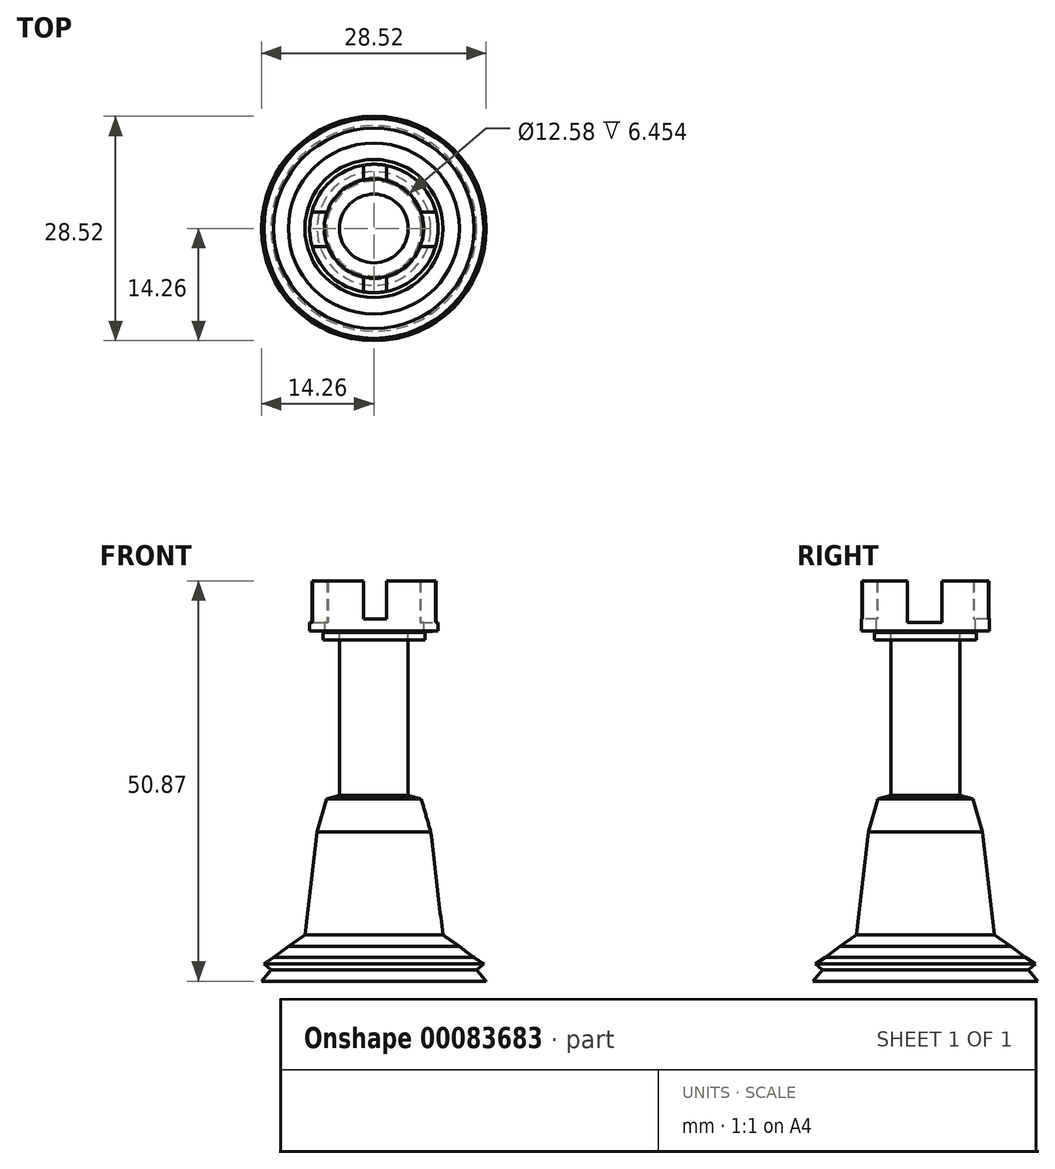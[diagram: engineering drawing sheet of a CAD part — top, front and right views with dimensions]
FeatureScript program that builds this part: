
annotation { "Feature Type Name" : "Feature", "Feature Type Description" : "" }
export const myFeature = defineFeature(function(context is Context, id is Id, definition is map)
    precondition{}
    {
        {
            var Q0;
            Q0=qCreatedBy(makeId("Front.planeOp"),FACE);
            var sketch = newSketch(context, id + "F0", { "sketchPlane" : qUnion([Q0])});
            skLineSegment(sketch, "E0", {"start": v(0, -44.34) * mm, "end": v(14.26, -44.34) * mm});
            skLineSegment(sketch, "E1", {"start": v(14.26, -44.34) * mm, "end": v(13.05, -42.87) * mm});
            skLineSegment(sketch, "E2", {"start": v(13.05, -42.87) * mm, "end": v(13.96, -42.13) * mm});
            skLineSegment(sketch, "E3", {"start": v(13.96, -42.13) * mm, "end": v(12.72, -41.33) * mm});
            skLineSegment(sketch, "E4", {"start": v(12.72, -41.33) * mm, "end": v(10.85, -39.9) * mm});
            skLineSegment(sketch, "E5", {"start": v(10.85, -39.9) * mm, "end": v(8.76, -38.47) * mm});
            skLineSegment(sketch, "E6", {"start": v(8.76, -38.47) * mm, "end": v(7.22, -25.38) * mm});
            skLineSegment(sketch, "E7", {"start": v(7.22, -25.38) * mm, "end": v(6.01, -21.2) * mm});
            skLineSegment(sketch, "E8", {"start": v(6.01, -21.2) * mm, "end": v(4.36, -20.75) * mm});
            skLineSegment(sketch, "E9", {"start": v(4.36, -20.75) * mm, "end": v(4.36, 0) * mm});
            skLineSegment(sketch, "E10", {"start": v(4.36, 0) * mm, "end": v(8.15, 0.16) * mm});
            skLineSegment(sketch, "E11", {"start": v(8.15, 0.16) * mm, "end": v(8.15, 6.53) * mm});
            skLineSegment(sketch, "E12", {"start": v(8.15, 6.53) * mm, "end": v(4.8, 6.53) * mm});
            skLineSegment(sketch, "E13", {"start": v(4.8, 6.53) * mm, "end": v(4.8, 2.9) * mm});
            skLineSegment(sketch, "E14", {"start": v(4.8, 2.9) * mm, "end": v(1.83, 2.9) * mm});
            skLineSegment(sketch, "E15", {"start": v(1.83, 2.9) * mm, "end": v(1.72, 6.64) * mm});
            skLineSegment(sketch, "E16", {"start": v(1.72, 6.64) * mm, "end": v(0, 6.6) * mm});
            skLineSegment(sketch, "E17", {"start": v(0, 6.6) * mm, "end": v(0, -44.34) * mm});
            skSolve(sketch);
        }
        {
            var Q0;
            Q0=makeQuery(id+"F0.imprint","IMPRINT",FACE,{"disambiguationData":[TD([[makeQuery(id+"F0.imprint","IMPRINT",EDGE,{"derivedFrom":sQuery(id+"F0.wireOp",EDGE,"E0")}),1.0]])]});
            var Q1;
            Q1=sQuery(id+"F0.wireOp",EDGE,"E17");
            revolve(context, id + "F1", {"entities" : qUnion([Q0]), "axis" : qUnion([Q1]), "revolveType" : RevolveType.FULL});
        }
        {
            var Q0;
            Q0=qCreatedBy(makeId("Top.planeOp"),FACE);
            var sketch = newSketch(context, id + "F2", { "sketchPlane" : qUnion([Q0])});
            skCircle(sketch, "E18", {"center": v(0, 0) * mm, "radius": 6.3 * mm});
            skSolve(sketch);
        }
        {
            var Q0;
            Q0 = qSketchRegion(id + "F2", true);
            var Q1;
            Q1=sQuery(id+"F2.wireOp",EDGE,"E18");
            extrude(context, id + "F3", {"entities" : qUnion([Q0]), "operationType" : NewBodyOperationType.REMOVE, "surfaceEntities" : qUnion([Q1]), "depth" : 25 * mm});
        }
        {
            var Q0;
            Q0=qCreatedBy(makeId("Front.planeOp"),FACE);
            var sketch = newSketch(context, id + "F4", { "sketchPlane" : qUnion([Q0])});
            skLineSegment(sketch, "E19.bottom", {"start": v(-1.32, 6.58) * mm, "end": v(1.61, 6.58) * mm});
            skLineSegment(sketch, "E19.top", {"start": v(-1.32, 1.72) * mm, "end": v(1.61, 1.72) * mm});
            skLineSegment(sketch, "E19.left", {"start": v(-1.32, 6.58) * mm, "end": v(-1.32, 1.72) * mm});
            skLineSegment(sketch, "E19.right", {"start": v(1.61, 6.58) * mm, "end": v(1.61, 1.72) * mm});
            skSolve(sketch);
        }
        {
            var Q0;
            Q0 = qSketchRegion(id + "F4", true);
            var Q1;
            Q1=sQuery(id+"F4.wireOp",EDGE,"E19.bottom");
            extrude(context, id + "F5", {"entities" : qUnion([Q0]), "operationType" : NewBodyOperationType.REMOVE, "surfaceEntities" : qUnion([Q1]), "oppositeDirection" : true, "depth" : 25 * mm, "hasSecondDirection" : true, "secondDirectionOppositeDirection" : false, "secondDirectionDepth" : 25 * mm});
        }
        {
            var Q0;
            Q0=qCreatedBy(makeId("Right.planeOp"),FACE);
            var sketch = newSketch(context, id + "F6", { "sketchPlane" : qUnion([Q0])});
            skLineSegment(sketch, "E20.bottom", {"start": v(2.11, 6.7) * mm, "end": v(-2.3, 6.7) * mm});
            skLineSegment(sketch, "E20.top", {"start": v(2.11, 1.24) * mm, "end": v(-2.3, 1.24) * mm});
            skLineSegment(sketch, "E20.left", {"start": v(2.11, 6.7) * mm, "end": v(2.11, 1.24) * mm});
            skLineSegment(sketch, "E20.right", {"start": v(-2.3, 6.7) * mm, "end": v(-2.3, 1.24) * mm});
            skSolve(sketch);
        }
        {
            var Q0;
            Q0 = qSketchRegion(id + "F6", true);
            var Q1;
            Q1=sQuery(id+"F6.wireOp",EDGE,"E20.bottom");
            extrude(context, id + "F7", {"entities" : qUnion([Q0]), "operationType" : NewBodyOperationType.REMOVE, "surfaceEntities" : qUnion([Q1]), "oppositeDirection" : true, "depth" : 25 * mm, "hasSecondDirection" : true, "secondDirectionOppositeDirection" : false, "secondDirectionDepth" : 25 * mm});
        }
        {
            var Q0;
            Q0=qCreatedBy(makeId("Top.planeOp"),FACE);
            var sketch = newSketch(context, id + "F8", { "sketchPlane" : qUnion([Q0])});
            skCircle(sketch, "E21", {"center": v(0, 0) * mm, "radius": 6.48 * mm});
            skSolve(sketch);
        }
        {
            var Q0;
            Q0 = qSketchRegion(id + "F8", true);
            var Q1;
            Q1=sQuery(id+"F8.wireOp",EDGE,"E21");
            extrude(context, id + "F9", {"entities" : qUnion([Q0]), "surfaceEntities" : qUnion([Q1]), "oppositeDirection" : true, "depth" : 1 * mm});
        }
    });
